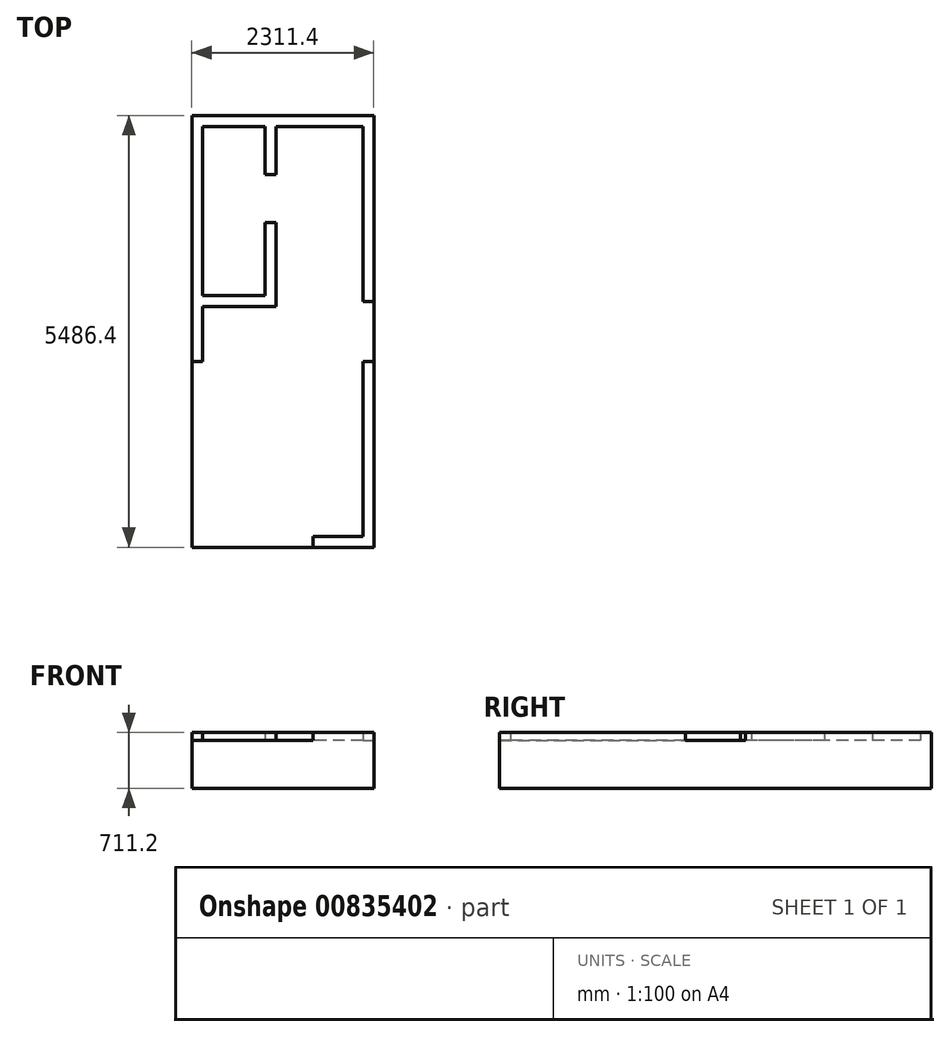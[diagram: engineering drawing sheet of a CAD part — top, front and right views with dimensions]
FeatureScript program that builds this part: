
annotation { "Feature Type Name" : "Feature", "Feature Type Description" : "" }
export const myFeature = defineFeature(function(context is Context, id is Id, definition is map)
    precondition{}
    {
        {
            var Q0;
            Q0=qCreatedBy(makeId("Top.planeOp"),FACE);
            var sketch = newSketch(context, id + "F0", { "sketchPlane" : qUnion([Q0])});
            skLineSegment(sketch, "E0.bottom", {"start": v(-1142.98, -679.46) * mm, "end": v(1168.42, -679.46) * mm});
            skLineSegment(sketch, "E0.top", {"start": v(-1142.98, 4806.94) * mm, "end": v(1168.42, 4806.94) * mm});
            skLineSegment(sketch, "E0.left", {"start": v(-1142.98, -679.46) * mm, "end": v(-1142.98, 4806.94) * mm});
            skLineSegment(sketch, "E0.right", {"start": v(1168.42, -679.46) * mm, "end": v(1168.42, 4806.94) * mm});
            skLineSegment(sketch, "E1.bottom", {"start": v(1168.42, -679.46) * mm, "end": v(1551.81, -679.46) * mm});
            skLineSegment(sketch, "E1.top", {"start": v(1168.42, -422.27) * mm, "end": v(1551.81, -422.27) * mm});
            skLineSegment(sketch, "E1.left", {"start": v(1168.42, -679.46) * mm, "end": v(1168.42, -422.27) * mm});
            skLineSegment(sketch, "E1.right", {"start": v(1551.81, -679.46) * mm, "end": v(1551.81, -422.27) * mm});
            skLineSegment(sketch, "E2.bottom", {"start": v(1551.81, -679.46) * mm, "end": v(694.7, -679.46) * mm});
            skLineSegment(sketch, "E2.top", {"start": v(1551.81, -859.23) * mm, "end": v(694.7, -859.23) * mm});
            skLineSegment(sketch, "E2.left", {"start": v(1551.81, -679.46) * mm, "end": v(1551.81, -859.23) * mm});
            skLineSegment(sketch, "E2.right", {"start": v(694.7, -679.46) * mm, "end": v(694.7, -859.23) * mm});
            skSolve(sketch);
        }
        {
            var Q0;
            {var subQ1=sQuery(id+"F0.wireOp",EDGE,"E0.top");Q0=makeQuery(id+"F0.imprint","IMPRINT",FACE,{"disambiguationData":[TD([[makeQuery(id+"F0.imprint","IMPRINT",EDGE,{"derivedFrom":subQ1}),-1.0]])]});}
            extrude(context, id + "F1", {"entities" : qUnion([Q0]), "depth" : 609.6 * mm, "offsetDistance" : 25.4 * mm});
        }
        {
            var Q0;
            Q0=makeQuery(id+"F1.opExtrude","CAP_FACE",FACE,{"disambiguationData":[OSD([sQuery(id+"F0.wireOp",EDGE,"E0.bottom"),sQuery(id+"F0.wireOp",EDGE,"E0.top"),sQuery(id+"F0.wireOp",EDGE,"E0.left"),sQuery(id+"F0.wireOp",EDGE,"E0.right")])],"isStart":false});
            var sketch = newSketch(context, id + "F2", { "sketchPlane" : qUnion([Q0])});
            skLineSegment(sketch, "E3.bottom", {"start": v(1028.72, 4667.24) * mm, "end": v(-1003.28, 4667.24) * mm});
            skLineSegment(sketch, "E3.top", {"start": v(1028.72, -539.76) * mm, "end": v(-1003.28, -539.76) * mm});
            skLineSegment(sketch, "E3.left", {"start": v(1028.72, 4667.24) * mm, "end": v(1028.72, -539.76) * mm});
            skLineSegment(sketch, "E3.right", {"start": v(-1003.28, 4667.24) * mm, "end": v(-1003.28, -539.76) * mm});
            skLineSegment(sketch, "E4.bottom", {"start": v(-1003.28, 4667.24) * mm, "end": v(-215.88, 4667.24) * mm});
            skLineSegment(sketch, "E4.top", {"start": v(-1003.28, 2520.94) * mm, "end": v(-215.88, 2520.94) * mm});
            skLineSegment(sketch, "E4.left", {"start": v(-1003.28, 4667.24) * mm, "end": v(-1003.28, 2520.94) * mm});
            skLineSegment(sketch, "E4.right", {"start": v(-215.88, 4667.24) * mm, "end": v(-215.88, 2520.94) * mm});
            skLineSegment(sketch, "E5.bottom", {"start": v(-1003.28, 4667.24) * mm, "end": v(-76.18, 4667.24) * mm});
            skLineSegment(sketch, "E5.top", {"start": v(-1003.28, 2381.24) * mm, "end": v(-76.18, 2381.24) * mm});
            skLineSegment(sketch, "E5.left", {"start": v(-1003.28, 4667.24) * mm, "end": v(-1003.28, 2381.24) * mm});
            skLineSegment(sketch, "E5.right", {"start": v(-76.18, 4667.24) * mm, "end": v(-76.18, 2381.24) * mm});
            skLineSegment(sketch, "E6.bottom", {"start": v(-215.88, 4057.64) * mm, "end": v(-76.18, 4057.64) * mm});
            skLineSegment(sketch, "E6.top", {"start": v(-215.88, 3448.04) * mm, "end": v(-76.18, 3448.04) * mm});
            skLineSegment(sketch, "E6.left", {"start": v(-215.88, 4057.64) * mm, "end": v(-215.88, 3448.04) * mm});
            skLineSegment(sketch, "E6.right", {"start": v(-76.18, 4057.64) * mm, "end": v(-76.18, 3448.04) * mm});
            skLineSegment(sketch, "E7.top", {"start": v(-368.28, -679.46) * mm, "end": v(393.72, -679.46) * mm});
            skLineSegment(sketch, "E7.right", {"start": v(393.72, -539.76) * mm, "end": v(393.72, -679.46) * mm});
            skLineSegment(sketch, "E8.bottom", {"start": v(-1003.28, 2444.74) * mm, "end": v(-1142.98, 2444.74) * mm});
            skLineSegment(sketch, "E8.top", {"start": v(-1003.28, 1682.74) * mm, "end": v(-1142.98, 1682.74) * mm});
            skLineSegment(sketch, "E8.left", {"start": v(-1003.28, 2444.74) * mm, "end": v(-1003.28, 1682.74) * mm});
            skLineSegment(sketch, "E8.right", {"start": v(-1142.98, 2444.74) * mm, "end": v(-1142.98, 1682.74) * mm});
            skLineSegment(sketch, "E9.bottom", {"start": v(1028.72, 2444.74) * mm, "end": v(1168.42, 2444.74) * mm});
            skLineSegment(sketch, "E9.top", {"start": v(1028.72, 1682.74) * mm, "end": v(1168.42, 1682.74) * mm});
            skLineSegment(sketch, "E9.left", {"start": v(1028.72, 2444.74) * mm, "end": v(1028.72, 1682.74) * mm});
            skLineSegment(sketch, "E9.right", {"start": v(1168.42, 2444.74) * mm, "end": v(1168.42, 1682.74) * mm});
            skSolve(sketch);
        }
        {
            var Q0;
            {var subQ5=sQuery(id+"F2.wireOp",EDGE,"E3.bottom");Q0=makeQuery(id+"F2.imprint","IMPRINT",FACE,{"disambiguationData":[TD([[makeQuery(id+"F2.imprint","IMPRINT",EDGE,{"derivedFrom":subQ5}),-1.0]])]});}
            var Q1;
            {var subQ3=sQuery(id+"F2.wireOp",EDGE,"E6.bottom");Q1=makeQuery(id+"F2.imprint","IMPRINT",FACE,{"disambiguationData":[TD([[makeQuery(id+"F2.imprint","IMPRINT",EDGE,{"derivedFrom":subQ3}),1.0]])]});}
            var Q2;
            {var subQ2=sQuery(id+"F2.wireOp",EDGE,"E4.top");Q2=makeQuery(id+"F2.imprint","IMPRINT",FACE,{"disambiguationData":[TD([[makeQuery(id+"F2.imprint","IMPRINT",EDGE,{"derivedFrom":subQ2}),-1.0]])]});}
            var Q3;
            {var subQ2=sQuery(id+"F2.wireOp",EDGE,"E3.right");Q3=makeQuery(id+"F2.imprint","IMPRINT",FACE,{"disambiguationData":[TD([[makeQuery(id+"F2.imprint","IMPRINT",EDGE,{"derivedFrom":subQ2}),-1.0]])]});}
            var Q4;
            Q4=makeQuery(id+"F2.imprint","IMPRINT",FACE,{"disambiguationData":[TD([[makeQuery(id+"F2.imprint","IMPRINT",EDGE,{"derivedFrom":sQuery(id+"F2.wireOp",EDGE,"E8.bottom")}),1.0]])]});
            var Q5;
            {var subQ1=sQuery(id+"F2.wireOp",EDGE,"E7.right");Q5=makeQuery(id+"F2.imprint","IMPRINT",FACE,{"disambiguationData":[TD([[makeQuery(id+"F2.imprint","IMPRINT",EDGE,{"derivedFrom":subQ1}),1.0]])]});}
            extrude(context, id + "F3", {"entities" : qUnion([Q0, Q1, Q2, Q3, Q4, Q5]), "operationType" : NewBodyOperationType.ADD, "depth" : 101.6 * mm, "offsetDistance" : 25.4 * mm});
        }
    });
